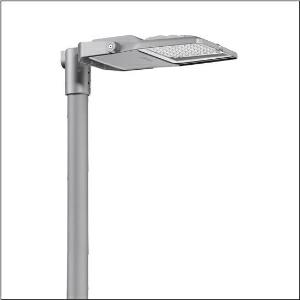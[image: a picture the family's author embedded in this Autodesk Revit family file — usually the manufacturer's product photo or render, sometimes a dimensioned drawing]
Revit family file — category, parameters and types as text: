
# Revit family: floodlight_fl_21_mini___pl43_5xa7776d2a3a_6ee6
name_source: partatom
category: Lighting Fixtures
units: mm (PartAtom-declared; Revit-internal decimal feet)

## family parameters
Cut with Voids When Loaded = No
Host = Face
Light Source = No
Part Type = Normal
Room Calculation Point = No
Round Connector Dimension = Use Diameter
Shared = No

## types (1)
- --- (1 x LED, 18300 lm, 142.9 W, 3000K)
    Apparent Load = 143 VA
    CIE Flux Codes = 27 78 99 100 100
    Color Rendering = 70
    Color Temperature = 3000K
    Default Elevation = 1800 mm
    Description = Floodlight FL 21 mini, floodlight, primary light control with lens, of PMMA, primary optical cover: protective disc, of toughened safety glass, transparent, light distribution: PL43, light emission: direct distribution, installation type: surface-mounted, LED, High Power LED, rated luminous flux: 18.300lm, luminous efficacy: 128lm/W, light colour: 730, colour temperature: 3000K, control: flexible luminous flux parameterisation, time-dependent luminous flux control, constant luminous flux control, overheat protection, presetting dimming logarithmic, with terminal, 6-pole, mains connection: 220..240V, AC, 50/60Hz, start of lifetime: 143W, end of service life: 151W, reduction: 63W, luminaire housing, of diecast aluminium, powder-coated, Siteco® metallic grey (DB 702S), corrosivity category C5 mid according to DIN EN ISO 12944, sealing non-destructively replaceable, please order mast flange separately, mast bracket, of steel, galvanised, powder-coated, Siteco® metallic grey (DB 702S), Smart Interface below and above, protection rating (complete): IP66, insulation class (complete): insulation class II (safety insulation), certification: CE, ENEC, VDE, protection symbol: D, impact resistance: IK08, permissible operating ambient temperature: -40..+40°C, permissible operating ambient temperature for outdoor applications: -40..+50°C, standard: DIN EN 12944, LABS conformity tested according to VDMA 24364:2018-05, packaging unit: 1 piece

Light Distribution: PL43
    Height = 70 mm
    Lamp = 1 x LED
    Lamp Light Flux = 18300 lm
    Lamp Power = 142.9 W
    Lamp count = 1
    Length = 485 mm
    Luminous efficacy = 128 lm/W
    Manufacturer = Siteco
    ModVariant = No
    Model = 5XA7776D2A3A
    Number of Poles = 1
    OnlyDefault = Yes
    Power Factor = 1
    Product Name = Floodlight FL 21 mini | PL43
    Product group = floodlight | pylon annexe
    ProductGroupID = 6200
    Protection Class = Protection class II
    Protection Degree = IP 66
    RLX_Detail_Level = 1
    RLX_Emergency_Light_Flux = 0 lm
    RLX_Emergency_Type = 0
    RLX_Emergency_Type_DB = No
    RlxData = <blob elided: 101269 chars, md5=a2c92342>
    Socket = socket
    Standby Power = 0 W
    System Light Flux = 18300 lm
    System Power = 143 W
    Type Comments = factory setting: luminous flux: 100 % | dim-lin: 254 | 730 mA
    Type Image = l_1007125.jpg
    URL = http://relux.com
    VarID = @adj_111103
    Voltage = 0 V
    Weight = 0.00 kg
    Width = 337 mm

## geometry (parser evidence)
native form markers: Blend x4, Sweep x14
no freeform markers — native parametric forms only
